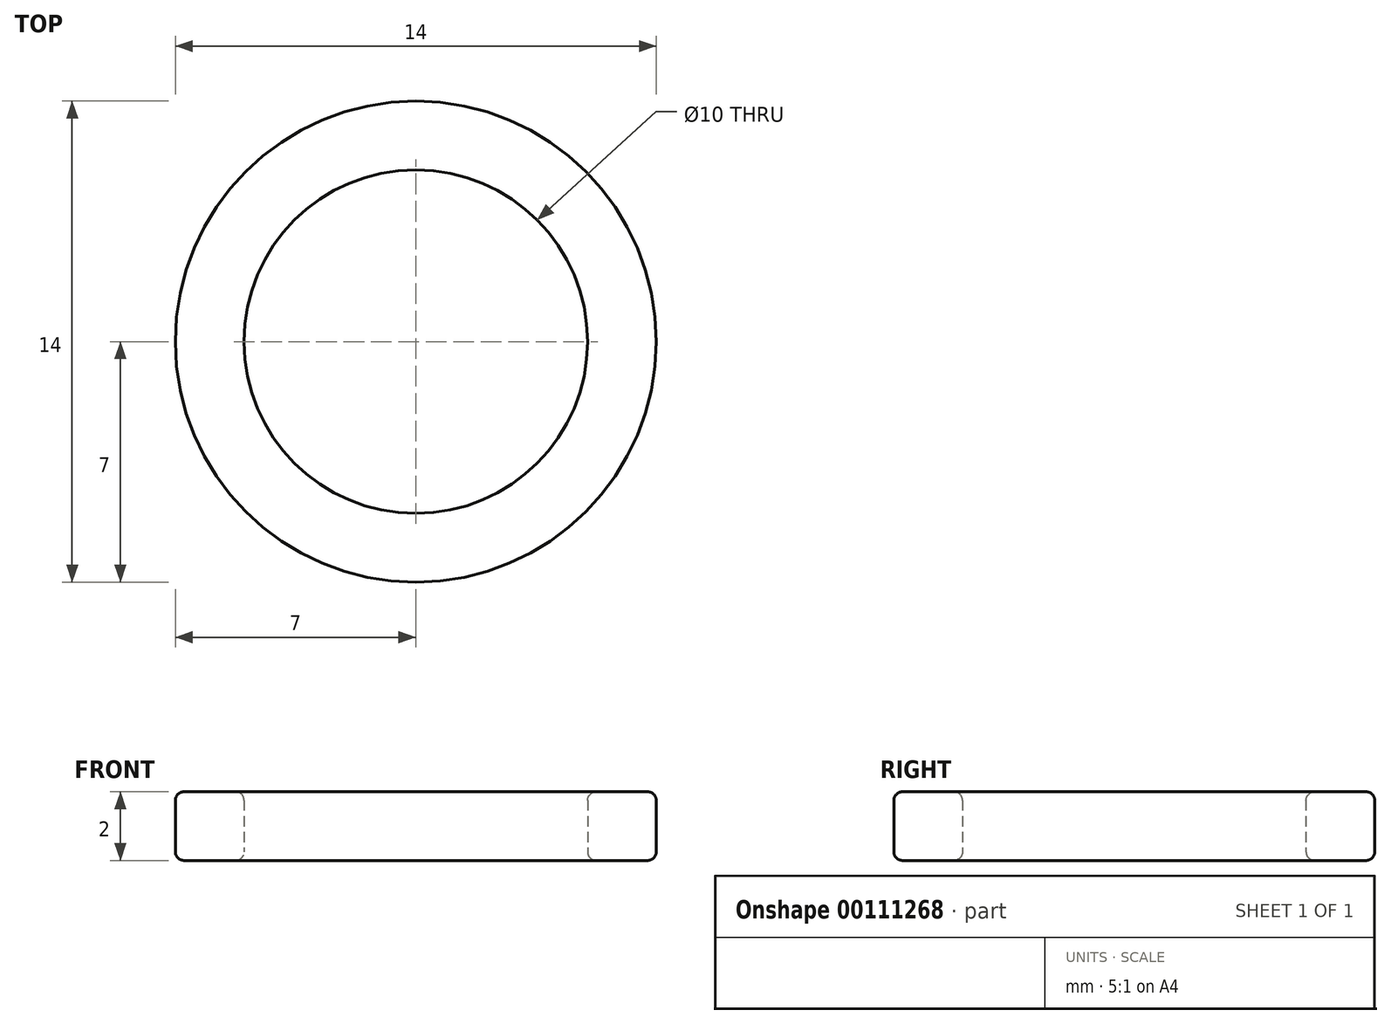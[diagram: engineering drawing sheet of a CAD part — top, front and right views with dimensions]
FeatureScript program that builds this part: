
annotation { "Feature Type Name" : "Feature", "Feature Type Description" : "" }
export const myFeature = defineFeature(function(context is Context, id is Id, definition is map)
    precondition{}
    {
        {
            var Q0;
            Q0=qCreatedBy(makeId("Top.planeOp"),FACE);
            var sketch = newSketch(context, id + "F0", { "sketchPlane" : qUnion([Q0])});
            skCircle(sketch, "E0", {"center": v(0, 0) * mm, "radius": 6 * mm, "construction": true});
            skSolve(sketch);
        }
        {
            var Q0;
            Q0=qCreatedBy(makeId("Right.planeOp"),FACE);
            var sketch = newSketch(context, id + "F1", { "sketchPlane" : qUnion([Q0])});
            skLineSegment(sketch, "E1.0", {"start": v(-6, 0) * mm, "end": v(6, 0) * mm, "construction": true});
            skLineSegment(sketch, "E2", {"start": v(0, 0) * mm, "end": v(0, 16.14) * mm, "construction": true});
            skLineSegment(sketch, "E3.bottom", {"start": v(5, 1) * mm, "end": v(7, 1) * mm});
            skLineSegment(sketch, "E3.top", {"start": v(5, -1) * mm, "end": v(7, -1) * mm});
            skLineSegment(sketch, "E3.left", {"start": v(5, 1) * mm, "end": v(5, -1) * mm});
            skLineSegment(sketch, "E3.right", {"start": v(7, 1) * mm, "end": v(7, -1) * mm});
            skPoint(sketch, "E3.middle", {"position": v(6, 0) * mm});
            skSolve(sketch);
        }
        {
            var Q0;
            Q0=makeQuery(id+"F1.imprint","IMPRINT",FACE,{"disambiguationData":[TD([[makeQuery(id+"F1.imprint","IMPRINT",EDGE,{"derivedFrom":sQuery(id+"F1.wireOp",EDGE,"E3.bottom")}),-1.0]])]});
            var Q1;
            Q1=sQuery(id+"F1.wireOp",EDGE,"E2");
            revolve(context, id + "F2", {"entities" : qUnion([Q0]), "axis" : qUnion([Q1]), "revolveType" : RevolveType.FULL});
        }
        {
            var Q0;
            Q0=makeQuery(id+"F2.opRevolve","SWEPT_EDGE",EDGE,{"disambiguationData":[OSD([sQuery(id+"F1.wireOp",EDGE,"E3.bottom"),sQuery(id+"F1.wireOp",EDGE,"E3.right")])]});
            var Q1;
            Q1=makeQuery(id+"F2.opRevolve","SWEPT_EDGE",EDGE,{"disambiguationData":[OSD([sQuery(id+"F1.wireOp",EDGE,"E3.bottom"),sQuery(id+"F1.wireOp",EDGE,"E3.left")])]});
            var Q2;
            Q2=makeQuery(id+"F2.opRevolve","SWEPT_EDGE",EDGE,{"disambiguationData":[OSD([sQuery(id+"F1.wireOp",EDGE,"E3.top"),sQuery(id+"F1.wireOp",EDGE,"E3.right")])]});
            var Q3;
            Q3=makeQuery(id+"F2.opRevolve","SWEPT_EDGE",EDGE,{"disambiguationData":[OSD([sQuery(id+"F1.wireOp",EDGE,"E3.top"),sQuery(id+"F1.wireOp",EDGE,"E3.left")])]});
            fillet(context, id + "F3", {"entities" : qUnion([Q0, Q1, Q2, Q3]), "radius" : 0.25 * mm, "tangentPropagation" : true, "allowEdgeOverflow" : false});
        }
    });
